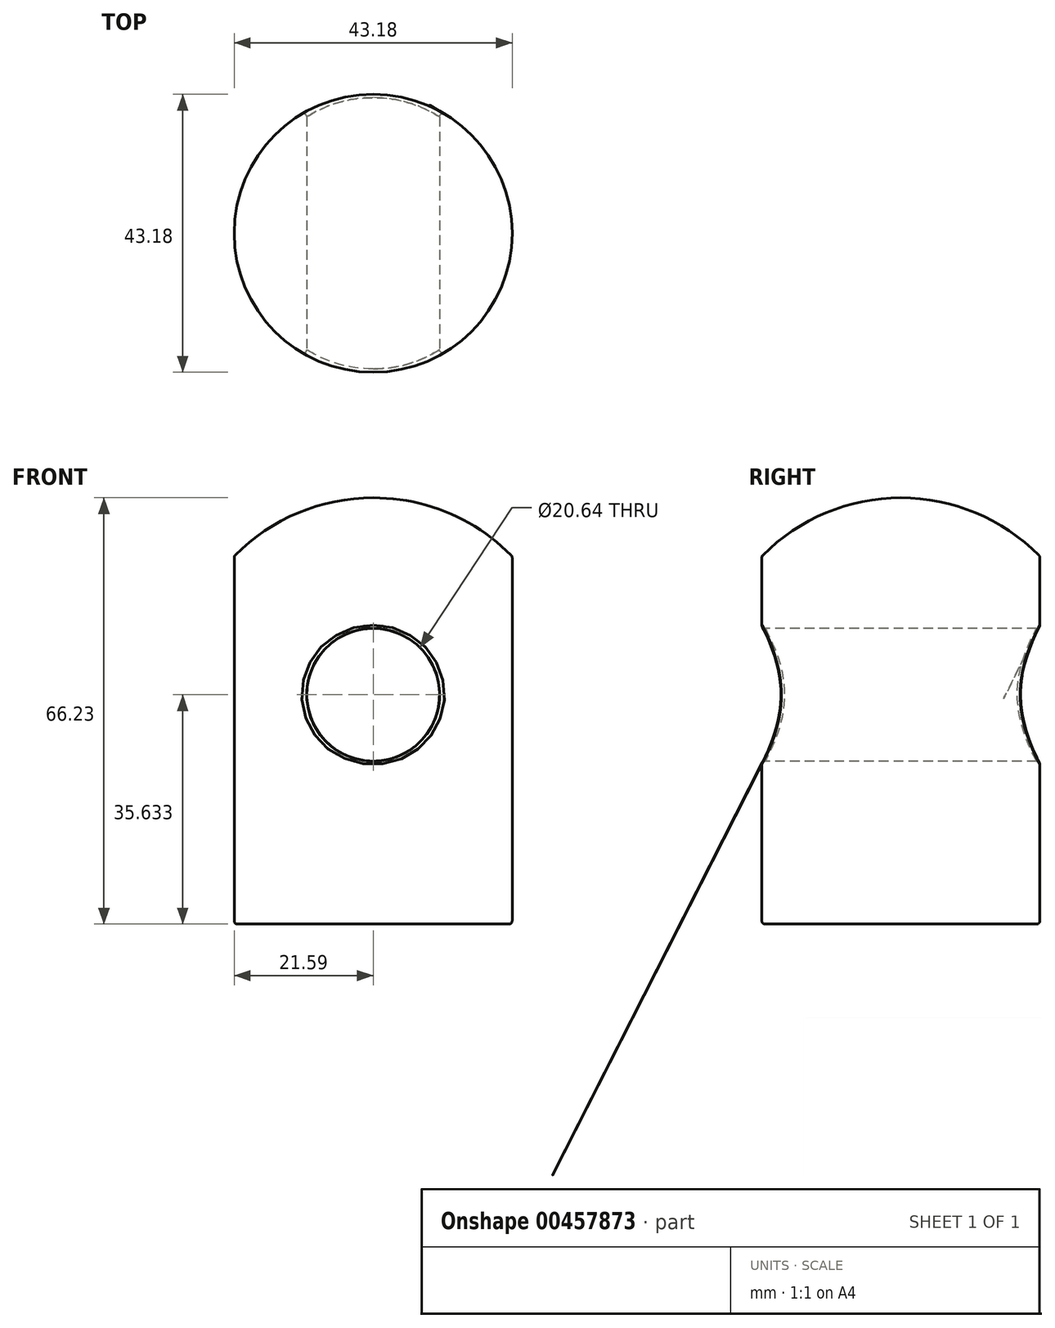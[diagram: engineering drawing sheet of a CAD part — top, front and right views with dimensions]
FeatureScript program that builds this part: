
annotation { "Feature Type Name" : "Feature", "Feature Type Description" : "" }
export const myFeature = defineFeature(function(context is Context, id is Id, definition is map)
    precondition{}
    {
        {
            var Q0;
            Q0=qCreatedBy(makeId("Front.planeOp"),FACE);
            var sketch = newSketch(context, id + "F0", { "sketchPlane" : qUnion([Q0])});
            skLineSegment(sketch, "E0", {"start": v(0, 10.87) * mm, "end": v(0, -55.42) * mm});
            skLineSegment(sketch, "E1", {"start": v(0, -55.42) * mm, "end": v(-21.59, -55.42) * mm});
            skLineSegment(sketch, "E2", {"start": v(-21.59, -55.42) * mm, "end": v(-21.59, 1.73) * mm});
            skArc(sketch, "E3", {"start": v(-21.59, 1.73) * mm, "mid": v(-11.71, 8.45) * mm, "end": v(0, 10.81) * mm});
            skPoint(sketch, "E4", {"position": v(0, -22.27) * mm});
            skSolve(sketch);
        }
        {
            var Q0;
            Q0=qCreatedBy(makeId("Front.planeOp"),FACE);
            var sketch = newSketch(context, id + "F1", { "sketchPlane" : qUnion([Q0])});
            skCircle(sketch, "E5", {"center": v(0, -19.79) * mm, "radius": 10.32 * mm});
            skSolve(sketch);
        }
        {
            var Q0;
            Q0 = qSketchRegion(id + "F0", true);
            var Q1;
            Q1=sQuery(id+"F0.wireOp",EDGE,"E0");
            revolve(context, id + "F2", {"entities" : qUnion([Q0]), "axis" : qUnion([Q1]), "revolveType" : RevolveType.FULL});
        }
        {
            var Q0;
            Q0 = qSketchRegion(id + "F1", true);
            extrude(context, id + "F3", {"entities" : qUnion([Q0]), "operationType" : NewBodyOperationType.REMOVE, "endBound" : BoundingType.THROUGH_ALL, "oppositeDirection" : true, "depth" : 25.4 * mm});
        }
        {
            var Q0;
            Q0 = qSketchRegion(id + "F1", true);
            extrude(context, id + "F4", {"entities" : qUnion([Q0]), "operationType" : NewBodyOperationType.REMOVE, "endBound" : BoundingType.THROUGH_ALL, "depth" : 25.4 * mm});
        }
        {
            var Q0;
            Q0=makeQuery(id+"F2.opRevolve","SWEPT_EDGE",EDGE,{"disambiguationData":[OSD([sQuery(id+"F0.wireOp",EDGE,"E2"),sQuery(id+"F0.wireOp",EDGE,"E3")])]});
            var Q1;
            Q1=makeQuery(id+"F4.boolean.opBoolean","INTERSECT",EDGE,{"derivedFrom":[makeQuery(id+"F2.opRevolve","SWEPT_FACE",FACE,{"disambiguationData":[OSD([sQuery(id+"F0.wireOp",EDGE,"E2")])]}),makeQuery(id+"F4.opExtrude","SWEPT_FACE",FACE,{"disambiguationData":[OSD([sQuery(id+"F1.wireOp",EDGE,"E5")])]})]});
            var Q2;
            Q2=makeQuery(id+"F2.opRevolve","SWEPT_EDGE",EDGE,{"disambiguationData":[OSD([sQuery(id+"F0.wireOp",EDGE,"E1"),sQuery(id+"F0.wireOp",EDGE,"E2")])]});
            var Q3;
            Q3=makeQuery(id+"F3.boolean.opBoolean","INTERSECT",EDGE,{"derivedFrom":[makeQuery(id+"F2.opRevolve","SWEPT_FACE",FACE,{"disambiguationData":[OSD([sQuery(id+"F0.wireOp",EDGE,"E2")])]}),makeQuery(id+"F3.opExtrude","SWEPT_FACE",FACE,{"disambiguationData":[OSD([sQuery(id+"F1.wireOp",EDGE,"E5")])]})]});
            fillet(context, id + "F5", {"entities" : qUnion([Q0, Q1, Q2, Q3]), "radius" : 0.5 * mm, "tangentPropagation" : true, "allowEdgeOverflow" : false});
        }
    });
